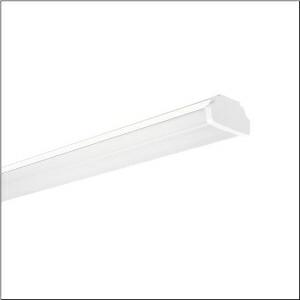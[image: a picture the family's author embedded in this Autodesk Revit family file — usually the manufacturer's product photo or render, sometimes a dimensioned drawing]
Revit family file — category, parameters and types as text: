
# Revit family: modario_r__31_mo_53bm812d2v4085_43f6
name_source: partatom
category: Lighting Fixtures
units: mm (PartAtom-declared; Revit-internal decimal feet)

## family parameters
Cut with Voids When Loaded = No
Host = Face
Light Source = No
Part Type = Normal
Room Calculation Point = No
Round Connector Dimension = Use Diameter
Shared = No

## types (1)
- --- (1 x LED, 8930 lm, 61.8 W, 4000K)
    Apparent Load = 62 VA
    CIE Flux Codes = 47 80 95 92 100
    Color Rendering = 80
    Color Temperature = 4000K
    Default Elevation = 1800 mm
    Description = Modario® 31 MOluminaire insert, length: 1.495mm, width: 81mm, height: 82mm, LED rated luminous flux: 8.930lm, light colour: 840, control gear: DALI 2, control gear: ECG DALI, with plug, 5-pole, with phase selection, mains connection: 220..240V, AC, 50/60Hz, primary optical cover: cover, of PMMA, light emission: direct distribution, primary light characteristic: symmetric, protection rating (complete): IP20, protection rating (LED compartment): IP50, insulation class (complete): insulation class I (protective earthing), certification: CE, ENEC, VDE, permissible ambient temperature for indoor applications: -25..+30°C, corresponds to IFS (International Featured Standards) requirements for safety and quality in the food industry, reducing of maximum allowable ambient temperature of 5°C with ceiling mounting, packaging unit: 1 piece
    Height = 92 mm
    Lamp = 1 x LED
    Lamp Light Flux = 8930 lm
    Lamp Power = 61.8 W
    Lamp count = 1
    Length = 1495 mm
    Luminous efficacy = 145 lm/W
    Manufacturer = Siteco
    ModVariant = No
    Model = 53BM812D2V4085
    Mounting Place = Ceiling
    Mounting Type = Pendant
    Number of Poles = 1
    OnlyDefault = Yes
    Power Factor = 1
    Product Name = Modario® 31 MO
    Product group = luminaire insert
    ProductGroupID = 902
    Protection Class = Protection class I
    Protection Degree = IP 20
    RLX_Detail_Level = 1
    RlxData = <blob elided: 42161 chars, md5=fa094f67>
    Socket = socket
    Standby Power = 0 W
    System Light Flux = 8930 lm
    System Power = 62 W
    Type Comments = factory setting: luminous flux: 100 % | dim-lin: 254 | 500 mA
    Type Image = l_1003447.jpg
    URL = http://relux.com
    VarID = @adj_117417
    Voltage = 0 V
    Weight = 0.00 kg
    Width = 81 mm

## geometry (parser evidence)
native form markers: Blend x4, Sweep x13
no freeform markers — native parametric forms only
